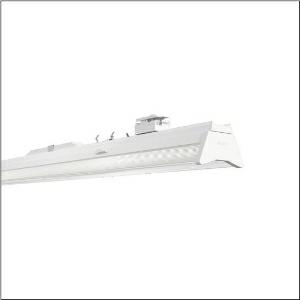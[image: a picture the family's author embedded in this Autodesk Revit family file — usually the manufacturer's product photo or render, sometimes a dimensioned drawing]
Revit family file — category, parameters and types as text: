
# Revit family: licross_r__21_performance_mo_52tm16dn4a5g_341e
name_source: partatom
category: Lighting Fixtures
units: mm (PartAtom-declared; Revit-internal decimal feet)

## family parameters
Cut with Voids When Loaded = No
Host = Face
Light Source = No
Part Type = Normal
Room Calculation Point = No
Round Connector Dimension = Use Diameter
Shared = No

## types (1)
- --- (1 x LED, 10840 lm, 62 W, 4000K)
    Apparent Load = 62 VA
    CIE Flux Codes = 66 88 96 79 100
    Color Rendering = 80
    Color Temperature = 4000K
    Default Elevation = 1800 mm
    Description = Licross® 21 Performance MO, luminaire insert, of sheet steel, galvanised, coil coated, white, length: 1.500mm, width: 120mm, height: 123mm, LED rated luminous flux: 10.840lm, light colour: 840, control gear: DALI 2, with plug, 5-pole, with phase selection, mains connection: 220..240V, AC, 50/60Hz, rated input power: 62W, halogen-free wiring, primary light control with lens, of plastic, primary optical cover: cover, of PMMA, light emission: direct/indirect distribution, primary light characteristic: symmetric, protection rating (complete): IP40, insulation class (complete): insulation class I (protective earthing), certification: CE, ENEC, UKCA, protection symbol: D if used in an environment without relevant dust loads with corresponding accessories, impact resistance: IK06, permissible ambient temperature for indoor applications: -25..+35°C, corresponds to IFS (International Featured Standards) requirements for safety and quality in the food industry, reducing of maximum allowable ambient temperature of 5°C with ceiling mounting, LABS conformity tested according to VDMA 24364:2018-05, packaging unit: 1 piece
    Height = 114 mm
    Lamp = 1 x LED
    Lamp Light Flux = 10840 lm
    Lamp Power = 62 W
    Lamp count = 1
    Length = 1500 mm
    Luminous efficacy = 175 lm/W
    Manufacturer = Siteco
    ModVariant = No
    Model = 52TM16DN4A5G
    Mounting Place = Ceiling
    Mounting Type = Pendant
    Number of Poles = 1
    OnlyDefault = Yes
    Power Factor = 1
    Product Name = Licross® 21 Performance MO
    Product group = luminaire insert
    ProductGroupID = 902
    Protection Class = Protection class I
    Protection Degree = IP 40
    RLX_Detail_Level = 1
    RLX_Emergency_Light_Flux = 0 lm
    RLX_Emergency_Type = 0
    RLX_Emergency_Type_DB = No
    RlxData = <blob elided: 34053 chars, md5=b5f3e561>
    Socket = socket
    Standby Power = 0 W
    System Light Flux = 10840 lm
    System Power = 62 W
    Type Comments = factory setting: luminous flux: 100 % | dim-lin: 254 | 418 mA
    Type Image = l_1256138.jpg
    URL = http://relux.com
    VarID = @adj_129226
    Voltage = 0 V
    Weight = 0.00 kg
    Width = 120 mm

## geometry (parser evidence)
native form markers: Blend x4, Sweep x11
no freeform markers — native parametric forms only
